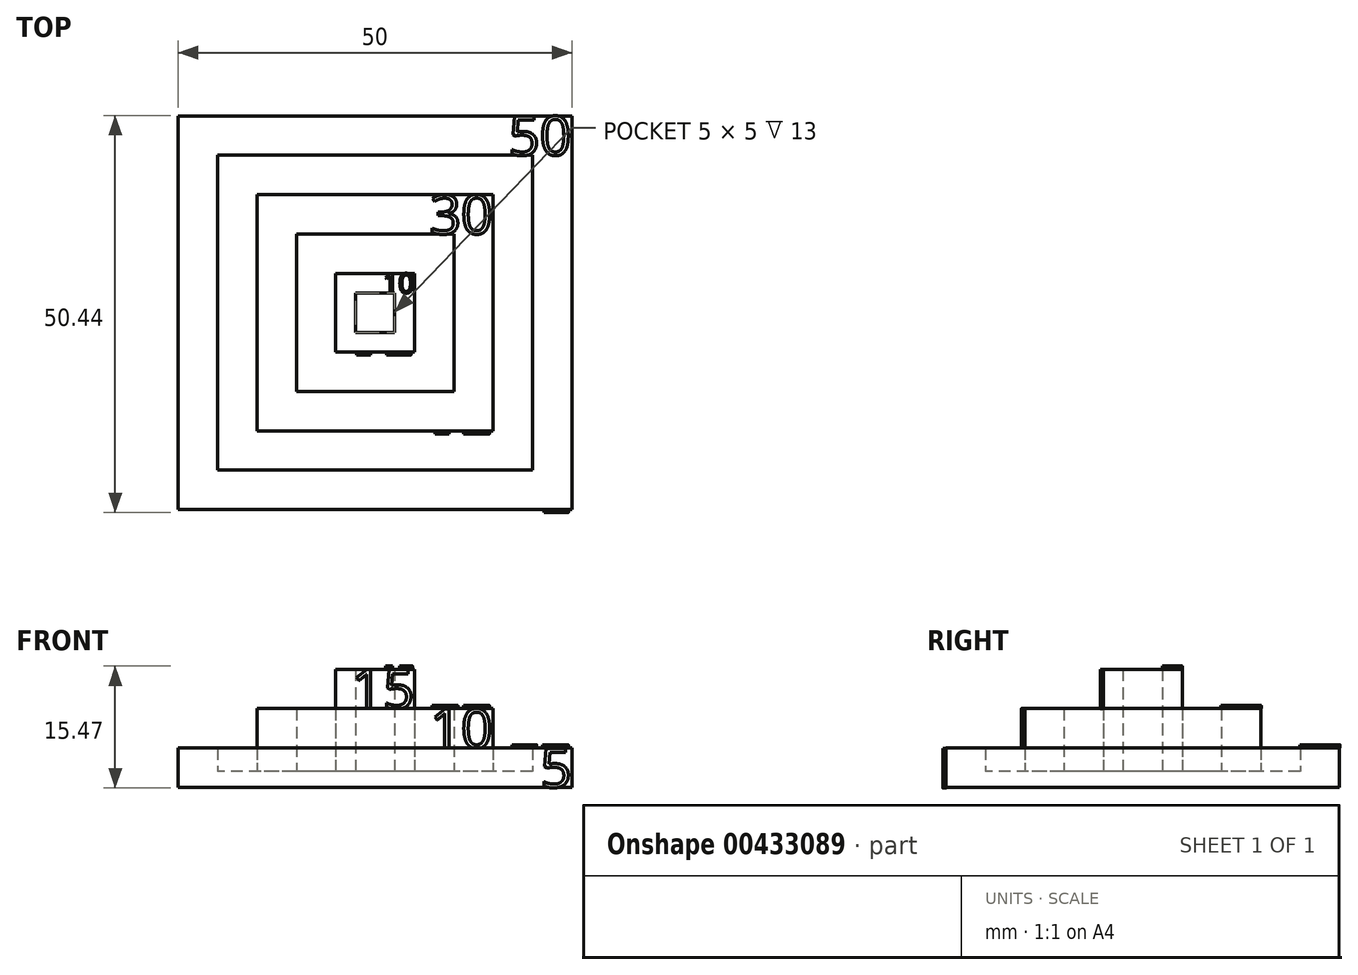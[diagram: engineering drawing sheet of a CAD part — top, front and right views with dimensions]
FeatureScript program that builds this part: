
annotation { "Feature Type Name" : "Feature", "Feature Type Description" : "" }
export const myFeature = defineFeature(function(context is Context, id is Id, definition is map)
    precondition{}
    {
        {
            var Q0;
            Q0=qCreatedBy(makeId("Top.planeOp"),FACE);
            var sketch = newSketch(context, id + "F0", { "sketchPlane" : qUnion([Q0])});
            skLineSegment(sketch, "E0.bottom", {"start": v(10, 10) * mm, "end": v(-10, 10) * mm});
            skLineSegment(sketch, "E0.top", {"start": v(10, -10) * mm, "end": v(-10, -10) * mm});
            skLineSegment(sketch, "E0.left", {"start": v(10, 10) * mm, "end": v(10, -10) * mm});
            skLineSegment(sketch, "E0.right", {"start": v(-10, 10) * mm, "end": v(-10, -10) * mm});
            skPoint(sketch, "E0.middle", {"position": v(0, 0) * mm});
            skLineSegment(sketch, "E1.bottom", {"start": v(5, 5) * mm, "end": v(-5, 5) * mm});
            skLineSegment(sketch, "E1.top", {"start": v(5, -5) * mm, "end": v(-5, -5) * mm});
            skLineSegment(sketch, "E1.left", {"start": v(5, 5) * mm, "end": v(5, -5) * mm});
            skLineSegment(sketch, "E1.right", {"start": v(-5, 5) * mm, "end": v(-5, -5) * mm});
            skLineSegment(sketch, "E2.bottom", {"start": v(2.5, 2.5) * mm, "end": v(-2.5, 2.5) * mm});
            skLineSegment(sketch, "E2.top", {"start": v(2.5, -2.5) * mm, "end": v(-2.5, -2.5) * mm});
            skLineSegment(sketch, "E2.left", {"start": v(2.5, 2.5) * mm, "end": v(2.5, -2.5) * mm});
            skLineSegment(sketch, "E2.right", {"start": v(-2.5, 2.5) * mm, "end": v(-2.5, -2.5) * mm});
            skLineSegment(sketch, "E3.bottom", {"start": v(25, 25) * mm, "end": v(-25, 25) * mm});
            skLineSegment(sketch, "E3.top", {"start": v(25, -25) * mm, "end": v(-25, -25) * mm});
            skLineSegment(sketch, "E3.left", {"start": v(25, 25) * mm, "end": v(25, -25) * mm});
            skLineSegment(sketch, "E3.right", {"start": v(-25, 25) * mm, "end": v(-25, -25) * mm});
            skLineSegment(sketch, "E4.bottom", {"start": v(15, 15) * mm, "end": v(-15, 15) * mm});
            skLineSegment(sketch, "E4.top", {"start": v(15, -15) * mm, "end": v(-15, -15) * mm});
            skLineSegment(sketch, "E4.left", {"start": v(15, 15) * mm, "end": v(15, -15) * mm});
            skLineSegment(sketch, "E4.right", {"start": v(-15, 15) * mm, "end": v(-15, -15) * mm});
            skLineSegment(sketch, "E5.bottom", {"start": v(20, 20) * mm, "end": v(-20, 20) * mm});
            skLineSegment(sketch, "E5.top", {"start": v(20, -20) * mm, "end": v(-20, -20) * mm});
            skLineSegment(sketch, "E5.left", {"start": v(20, 20) * mm, "end": v(20, -20) * mm});
            skLineSegment(sketch, "E5.right", {"start": v(-20, 20) * mm, "end": v(-20, -20) * mm});
            skSolve(sketch);
        }
        {
            var Q0;
            Q0=makeQuery(id+"F0.imprint","IMPRINT",FACE,{"disambiguationData":[TD([[makeQuery(id+"F0.imprint","IMPRINT",EDGE,{"derivedFrom":sQuery(id+"F0.wireOp",EDGE,"E1.bottom")}),1.0]])]});
            var Q1;
            Q1=makeQuery(id+"F0.imprint","IMPRINT",FACE,{"disambiguationData":[TD([[makeQuery(id+"F0.imprint","IMPRINT",EDGE,{"derivedFrom":sQuery(id+"F0.wireOp",EDGE,"E0.bottom")}),-1.0]])]});
            var Q2;
            Q2=makeQuery(id+"F0.imprint","IMPRINT",FACE,{"disambiguationData":[TD([[makeQuery(id+"F0.imprint","IMPRINT",EDGE,{"derivedFrom":sQuery(id+"F0.wireOp",EDGE,"E0.bottom")}),1.0]])]});
            var Q3;
            Q3=makeQuery(id+"F0.imprint","IMPRINT",FACE,{"disambiguationData":[TD([[makeQuery(id+"F0.imprint","IMPRINT",EDGE,{"derivedFrom":sQuery(id+"F0.wireOp",EDGE,"E2.bottom")}),1.0]])]});
            var Q4;
            Q4=makeQuery(id+"F0.imprint","IMPRINT",FACE,{"disambiguationData":[TD([[makeQuery(id+"F0.imprint","IMPRINT",EDGE,{"derivedFrom":sQuery(id+"F0.wireOp",EDGE,"E4.bottom")}),-1.0]])]});
            var Q5;
            Q5=makeQuery(id+"F0.imprint","IMPRINT",FACE,{"disambiguationData":[TD([[makeQuery(id+"F0.imprint","IMPRINT",EDGE,{"derivedFrom":sQuery(id+"F0.wireOp",EDGE,"E3.bottom")}),1.0]])]});
            extrude(context, id + "F1", {"entities" : qUnion([Q0, Q1, Q2, Q3, Q4, Q5]), "oppositeDirection" : true, "depth" : 2 * mm});
        }
        {
            var Q0;
            Q0=makeQuery(id+"F0.imprint","IMPRINT",FACE,{"disambiguationData":[TD([[makeQuery(id+"F0.imprint","IMPRINT",EDGE,{"derivedFrom":sQuery(id+"F0.wireOp",EDGE,"E0.bottom")}),-1.0]])]});
            var Q1;
            Q1=makeQuery(id+"F0.imprint","IMPRINT",FACE,{"disambiguationData":[TD([[makeQuery(id+"F0.imprint","IMPRINT",EDGE,{"derivedFrom":sQuery(id+"F0.wireOp",EDGE,"E1.bottom")}),1.0]])]});
            var Q2;
            Q2=makeQuery(id+"F0.imprint","IMPRINT",FACE,{"disambiguationData":[TD([[makeQuery(id+"F0.imprint","IMPRINT",EDGE,{"derivedFrom":sQuery(id+"F0.wireOp",EDGE,"E3.bottom")}),1.0]])]});
            extrude(context, id + "F2", {"entities" : qUnion([Q0, Q1, Q2]), "operationType" : NewBodyOperationType.ADD, "depth" : 3 * mm});
        }
        {
            var Q0;
            Q0=makeQuery(id+"F2.opExtrude","CAP_FACE",FACE,{"disambiguationData":[OSD([sQuery(id+"F0.wireOp",EDGE,"E0.bottom"),sQuery(id+"F0.wireOp",EDGE,"E0.top"),sQuery(id+"F0.wireOp",EDGE,"E0.left"),sQuery(id+"F0.wireOp",EDGE,"E0.right"),sQuery(id+"F0.wireOp",EDGE,"E4.bottom"),sQuery(id+"F0.wireOp",EDGE,"E4.top"),sQuery(id+"F0.wireOp",EDGE,"E4.left"),sQuery(id+"F0.wireOp",EDGE,"E4.right")])],"isStart":false});
            extrude(context, id + "F3", {"entities" : qUnion([Q0]), "operationType" : NewBodyOperationType.ADD, "depth" : 5 * mm});
        }
        {
            var Q0;
            Q0=makeQuery(id+"F2.opExtrude","CAP_FACE",FACE,{"disambiguationData":[OSD([sQuery(id+"F0.wireOp",EDGE,"E1.bottom"),sQuery(id+"F0.wireOp",EDGE,"E1.top"),sQuery(id+"F0.wireOp",EDGE,"E1.left"),sQuery(id+"F0.wireOp",EDGE,"E1.right"),sQuery(id+"F0.wireOp",EDGE,"E2.bottom"),sQuery(id+"F0.wireOp",EDGE,"E2.top"),sQuery(id+"F0.wireOp",EDGE,"E2.left"),sQuery(id+"F0.wireOp",EDGE,"E2.right")])],"isStart":false});
            extrude(context, id + "F4", {"entities" : qUnion([Q0]), "operationType" : NewBodyOperationType.ADD, "depth" : 10 * mm});
        }
        {
            var Q0;
            {var subQ0=sQuery(id+"F0.wireOp",EDGE,"E3.top");Q0=makeQuery(id+"F2.boolean.opBoolean","MERGE",FACE,{"derivedFrom":[makeQuery(id+"F1.opExtrude","SWEPT_FACE",FACE,{"disambiguationData":[OSD([subQ0])]}),makeQuery(id+"F2.opExtrude","SWEPT_FACE",FACE,{"disambiguationData":[OSD([subQ0])]})]});}
            var sketch = newSketch(context, id + "F5", { "sketchPlane" : qUnion([Q0])});
            skText(sketch, "E6", { "text": "5", "fontName": "OpenSans-Regular.ttf"});
            const initialGuessF5  = {"E6": [0.02098, -0.002, 1, 0, 0.005]};
            skSetInitialGuess(sketch, initialGuessF5);
            skSolve(sketch);
        }
        {
            var Q0;
            {var subQ0=sQuery(id+"F0.wireOp",EDGE,"E4.top");Q0=makeQuery(id+"F3.boolean.opBoolean","MERGE",FACE,{"derivedFrom":[makeQuery(id+"F2.opExtrude","SWEPT_FACE",FACE,{"disambiguationData":[OSD([subQ0])]}),makeQuery(id+"F3.opExtrude","SWEPT_FACE",FACE,{"disambiguationData":[OSD([subQ0])]})]});}
            var sketch = newSketch(context, id + "F6", { "sketchPlane" : qUnion([Q0])});
            skText(sketch, "E7", { "text": "10", "fontName": "OpenSans-Regular.ttf"});
            const initialGuessF6  = {"E7": [0.00695, 0.003, 1, 0, 0.005]};
            skSetInitialGuess(sketch, initialGuessF6);
            skSolve(sketch);
        }
        {
            var Q0;
            {var subQ0=sQuery(id+"F0.wireOp",EDGE,"E1.top");Q0=makeQuery(id+"F4.boolean.opBoolean","MERGE",FACE,{"derivedFrom":[makeQuery(id+"F2.opExtrude","SWEPT_FACE",FACE,{"disambiguationData":[OSD([subQ0])]}),makeQuery(id+"F4.opExtrude","SWEPT_FACE",FACE,{"disambiguationData":[OSD([subQ0])]})]});}
            var sketch = newSketch(context, id + "F7", { "sketchPlane" : qUnion([Q0])});
            skText(sketch, "E8", { "text": "15", "fontName": "OpenSans-Regular.ttf"});
            const initialGuessF7  = {"E8": [-0.00298, 0.008, 1, 0, 0.005]};
            skSetInitialGuess(sketch, initialGuessF7);
            skSolve(sketch);
        }
        {
            var Q0;
            Q0=makeQuery(id+"F2.opExtrude","CAP_FACE",FACE,{"disambiguationData":[OSD([sQuery(id+"F0.wireOp",EDGE,"E3.bottom"),sQuery(id+"F0.wireOp",EDGE,"E3.top"),sQuery(id+"F0.wireOp",EDGE,"E3.left"),sQuery(id+"F0.wireOp",EDGE,"E3.right"),sQuery(id+"F0.wireOp",EDGE,"E5.bottom"),sQuery(id+"F0.wireOp",EDGE,"E5.top"),sQuery(id+"F0.wireOp",EDGE,"E5.left"),sQuery(id+"F0.wireOp",EDGE,"E5.right")])],"isStart":false});
            var sketch = newSketch(context, id + "F8", { "sketchPlane" : qUnion([Q0])});
            skText(sketch, "E9", { "text": "50", "fontName": "OpenSans-Regular.ttf"});
            const initialGuessF8  = {"E9": [0.01695, 0.02, 1, 0, 0.005]};
            skSetInitialGuess(sketch, initialGuessF8);
            skSolve(sketch);
        }
        {
            var Q0;
            Q0=makeQuery(id+"F3.opExtrude","CAP_FACE",FACE,{"disambiguationData":[OSD([sQuery(id+"F0.wireOp",EDGE,"E0.bottom"),sQuery(id+"F0.wireOp",EDGE,"E0.top"),sQuery(id+"F0.wireOp",EDGE,"E0.left"),sQuery(id+"F0.wireOp",EDGE,"E0.right"),sQuery(id+"F0.wireOp",EDGE,"E4.bottom"),sQuery(id+"F0.wireOp",EDGE,"E4.top"),sQuery(id+"F0.wireOp",EDGE,"E4.left"),sQuery(id+"F0.wireOp",EDGE,"E4.right")])],"isStart":false});
            var sketch = newSketch(context, id + "F9", { "sketchPlane" : qUnion([Q0])});
            skText(sketch, "E10", { "text": "30", "fontName": "OpenSans-Regular.ttf"});
            const initialGuessF9  = {"E10": [0.00695, 0.01, 1, 0, 0.005]};
            skSetInitialGuess(sketch, initialGuessF9);
            skSolve(sketch);
        }
        {
            var Q0;
            Q0=makeQuery(id+"F4.opExtrude","CAP_FACE",FACE,{"disambiguationData":[OSD([sQuery(id+"F0.wireOp",EDGE,"E1.bottom"),sQuery(id+"F0.wireOp",EDGE,"E1.top"),sQuery(id+"F0.wireOp",EDGE,"E1.left"),sQuery(id+"F0.wireOp",EDGE,"E1.right"),sQuery(id+"F0.wireOp",EDGE,"E2.bottom"),sQuery(id+"F0.wireOp",EDGE,"E2.top"),sQuery(id+"F0.wireOp",EDGE,"E2.left"),sQuery(id+"F0.wireOp",EDGE,"E2.right")])],"isStart":false});
            var sketch = newSketch(context, id + "F10", { "sketchPlane" : qUnion([Q0])});
            skText(sketch, "E11", { "text": "10", "fontName": "OpenSans-Regular.ttf"});
            const initialGuessF10  = {"E11": [0.00098, 0.0025, 1, 0, 0.0025]};
            skSetInitialGuess(sketch, initialGuessF10);
            skSolve(sketch);
        }
        {
            var Q0;
            Q0 = qSketchRegion(id + "F8", true);
            var Q1;
            Q1 = qSketchRegion(id + "F9", true);
            var Q2;
            Q2 = qSketchRegion(id + "F10", true);
            extrude(context, id + "F11", {"entities" : qUnion([Q0, Q1, Q2]), "operationType" : NewBodyOperationType.ADD, "depth" : 0.4 * mm});
        }
        {
            var Q0;
            Q0 = qSketchRegion(id + "F5", true);
            var Q1;
            Q1 = qSketchRegion(id + "F6", true);
            var Q2;
            Q2 = qSketchRegion(id + "F7", true);
            extrude(context, id + "F12", {"entities" : qUnion([Q0, Q1, Q2]), "operationType" : NewBodyOperationType.ADD, "depth" : 0.4 * mm});
        }
    });
